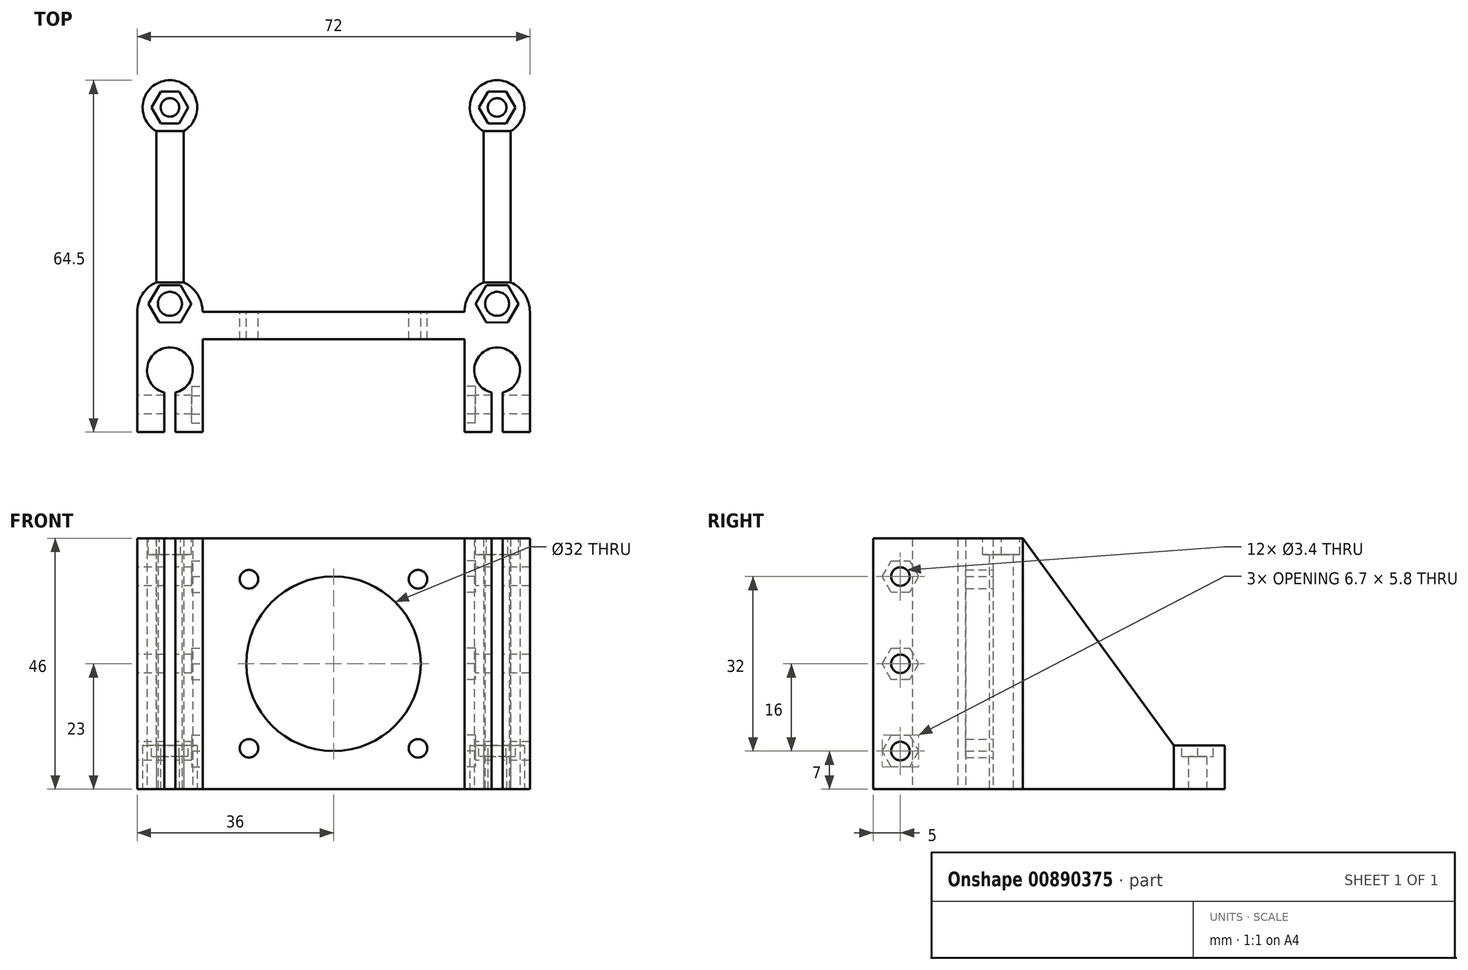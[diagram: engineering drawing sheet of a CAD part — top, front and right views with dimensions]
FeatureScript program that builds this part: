
annotation { "Feature Type Name" : "Feature", "Feature Type Description" : "" }
export const myFeature = defineFeature(function(context is Context, id is Id, definition is map)
    precondition{}
    {
        {
            var Q0;
            Q0=qCreatedBy(makeId("Top.planeOp"),FACE);
            var sketch = newSketch(context, id + "F0", { "sketchPlane" : qUnion([Q0])});
            skArc(sketch, "E0", {"start": v(-29, -14.78) * mm, "mid": v(-30, -6.5) * mm, "end": v(-31, -14.78) * mm});
            skPoint(sketch, "E1.first.point", {"position": v(-36, 0) * mm});
            skLineSegment(sketch, "E2", {"start": v(-36, 0) * mm, "end": v(-36, -22) * mm});
            skLineSegment(sketch, "E3", {"start": v(-36, -22) * mm, "end": v(-31, -22) * mm});
            skLineSegment(sketch, "E4", {"start": v(-31, -22) * mm, "end": v(-31, -14.78) * mm});
            skLineSegment(sketch, "E5", {"start": v(-29, -14.78) * mm, "end": v(-29, -22) * mm});
            skLineSegment(sketch, "E6", {"start": v(-29, -22) * mm, "end": v(-24, -22) * mm});
            skLineSegment(sketch, "E7", {"start": v(0, 0) * mm, "end": v(-24, 0) * mm});
            skLineSegment(sketch, "E8", {"start": v(0, 0) * mm, "end": v(0, -5) * mm});
            skLineSegment(sketch, "E9", {"start": v(0, -5) * mm, "end": v(-24, -5) * mm});
            skLineSegment(sketch, "E10", {"start": v(-24, -5) * mm, "end": v(-24, -22) * mm});
            skLineSegment(sketch, "E11", {"start": v(-30, -10.7) * mm, "end": v(-30, 1.5) * mm, "construction": true});
            skLineSegment(sketch, "E12", {"start": v(-24, 0) * mm, "end": v(-36, 0) * mm, "construction": true});
            skArc(sketch, "E13", {"start": v(-24, 0) * mm, "mid": v(-30, 6) * mm, "end": v(-36, 0) * mm});
            skLineSegment(sketch, "E14.MirrorCS", {"start": v(0, -5) * mm, "end": v(24, -5) * mm});
            skLineSegment(sketch, "E15.MirrorCS", {"start": v(24, 0) * mm, "end": v(36, 0) * mm, "construction": true});
            skLineSegment(sketch, "E16.MirrorCS", {"start": v(29, -22) * mm, "end": v(24, -22) * mm});
            skLineSegment(sketch, "E17.MirrorCS", {"start": v(31, -22) * mm, "end": v(31, -14.78) * mm});
            skLineSegment(sketch, "E18.MirrorCS", {"start": v(29, -14.78) * mm, "end": v(29, -22) * mm});
            skPoint(sketch, "E19.MirrorP", {"position": v(36, 0) * mm});
            skArc(sketch, "E20.MirrorCS", {"start": v(24, 0) * mm, "mid": v(30, 6) * mm, "end": v(36, 0) * mm});
            skArc(sketch, "E21.MirrorC", {"start": v(29, -14.78) * mm, "mid": v(30, -6.5) * mm, "end": v(31, -14.78) * mm});
            skLineSegment(sketch, "E22.MirrorCS", {"start": v(0, 0) * mm, "end": v(24, 0) * mm});
            skLineSegment(sketch, "E23.MirrorCS", {"start": v(24, -5) * mm, "end": v(24, -22) * mm});
            skLineSegment(sketch, "E24.MirrorCS", {"start": v(30, -10.7) * mm, "end": v(30, 1.5) * mm, "construction": true});
            skLineSegment(sketch, "E25.MirrorCS", {"start": v(36, -22) * mm, "end": v(31, -22) * mm});
            skLineSegment(sketch, "E26.MirrorCS", {"start": v(36, 0) * mm, "end": v(36, -22) * mm});
            skCircle(sketch, "E27", {"center": v(-30, 1.5) * mm, "radius": 2.2 * mm});
            skCircle(sketch, "E28.MirrorC", {"center": v(30, 1.5) * mm, "radius": 2.2 * mm});
            skLineSegment(sketch, "E29", {"start": v(-30, 1.5) * mm, "end": v(-30, 46.69) * mm, "construction": true});
            skLineSegment(sketch, "E30", {"start": v(-32.5, 5.45) * mm, "end": v(-32.5, 33.17) * mm});
            skLineSegment(sketch, "E31", {"start": v(-32.5, 33.17) * mm, "end": v(-27.5, 33.17) * mm});
            skLineSegment(sketch, "E32", {"start": v(-27.5, 33.17) * mm, "end": v(-27.5, 5.45) * mm});
            skLineSegment(sketch, "E33", {"start": v(-27.5, 5.45) * mm, "end": v(-32.5, 5.45) * mm, "construction": true});
            skCircle(sketch, "E34", {"center": v(-30, 37.5) * mm, "radius": 1.7 * mm});
            skCircle(sketch, "E35", {"center": v(-30, 37.5) * mm, "radius": 5 * mm});
            skLineSegment(sketch, "E36.MirrorCS", {"start": v(27.5, 33.17) * mm, "end": v(27.5, 5.45) * mm});
            skLineSegment(sketch, "E37.MirrorCS", {"start": v(32.5, 5.45) * mm, "end": v(32.5, 33.17) * mm});
            skCircle(sketch, "E38.MirrorC", {"center": v(30, 37.5) * mm, "radius": 5 * mm});
            skCircle(sketch, "E39.MirrorC", {"center": v(30, 37.5) * mm, "radius": 1.7 * mm});
            skSolve(sketch);
        }
        {
            var Q0;
            Q0=qSketchRegion(id+"F0",true);
            extrude(context, id + "F1", {"entities" : qUnion([Q0]), "depth" : 46 * mm, "offsetDistance" : 25 * mm});
        }
        {
            var Q0;
            Q0=makeQuery(id+"F1.opExtrude","CAP_FACE",FACE,{"disambiguationData":[OSD([sQuery(id+"F0.wireOp",EDGE,"E0"),sQuery(id+"F0.wireOp",EDGE,"E2"),sQuery(id+"F0.wireOp",EDGE,"E3"),sQuery(id+"F0.wireOp",EDGE,"E4"),sQuery(id+"F0.wireOp",EDGE,"E5"),sQuery(id+"F0.wireOp",EDGE,"E6"),sQuery(id+"F0.wireOp",EDGE,"E7"),sQuery(id+"F0.wireOp",EDGE,"E9"),sQuery(id+"F0.wireOp",EDGE,"E10"),sQuery(id+"F0.wireOp",EDGE,"E13"),sQuery(id+"F0.wireOp",EDGE,"E14.MirrorCS"),sQuery(id+"F0.wireOp",EDGE,"E16.MirrorCS"),sQuery(id+"F0.wireOp",EDGE,"E17.MirrorCS"),sQuery(id+"F0.wireOp",EDGE,"E18.MirrorCS"),sQuery(id+"F0.wireOp",EDGE,"E20.MirrorCS"),sQuery(id+"F0.wireOp",EDGE,"E21.MirrorC"),sQuery(id+"F0.wireOp",EDGE,"E22.MirrorCS"),sQuery(id+"F0.wireOp",EDGE,"E23.MirrorCS"),sQuery(id+"F0.wireOp",EDGE,"E25.MirrorCS"),sQuery(id+"F0.wireOp",EDGE,"E26.MirrorCS"),sQuery(id+"F0.wireOp",EDGE,"E27"),sQuery(id+"F0.wireOp",EDGE,"E28.MirrorC")])],"isStart":false});
            var sketch = newSketch(context, id + "F2", { "sketchPlane" : qUnion([Q0])});
            skCircle(sketch, "E40.cCircle", {"center": v(-30, 1.5) * mm, "radius": 3.4 * mm, "construction": true});
            skLineSegment(sketch, "E40.0", {"start": v(-26.07, 1.48) * mm, "end": v(-28.05, -1.9) * mm});
            skLineSegment(sketch, "E40.1", {"start": v(-28.05, -1.9) * mm, "end": v(-31.98, -1.9) * mm});
            skLineSegment(sketch, "E40.2", {"start": v(-31.98, -1.9) * mm, "end": v(-33.93, 1.52) * mm});
            skLineSegment(sketch, "E40.3", {"start": v(-33.93, 1.52) * mm, "end": v(-31.95, 4.9) * mm});
            skLineSegment(sketch, "E40.4", {"start": v(-31.95, 4.9) * mm, "end": v(-28.02, 4.9) * mm});
            skLineSegment(sketch, "E40.5", {"start": v(-28.02, 4.9) * mm, "end": v(-26.07, 1.48) * mm});
            skPoint(sketch, "E40.0.midPoint", {"position": v(-27.06, -0.21) * mm});
            skPoint(sketch, "E41.MirrorP", {"position": v(27.06, -0.21) * mm});
            skLineSegment(sketch, "E42.MirrorCS", {"start": v(31.95, 4.9) * mm, "end": v(28.02, 4.9) * mm});
            skLineSegment(sketch, "E43.MirrorCS", {"start": v(28.05, -1.9) * mm, "end": v(31.98, -1.9) * mm});
            skLineSegment(sketch, "E44.MirrorCS", {"start": v(31.98, -1.9) * mm, "end": v(33.93, 1.52) * mm});
            skCircle(sketch, "E45.MirrorC", {"center": v(30, 1.5) * mm, "radius": 3.4 * mm, "construction": true});
            skLineSegment(sketch, "E46.MirrorCS", {"start": v(26.07, 1.48) * mm, "end": v(28.05, -1.9) * mm});
            skLineSegment(sketch, "E47.MirrorCS", {"start": v(33.93, 1.52) * mm, "end": v(31.95, 4.9) * mm});
            skLineSegment(sketch, "E48.MirrorCS", {"start": v(28.02, 4.9) * mm, "end": v(26.07, 1.48) * mm});
            skSolve(sketch);
        }
        {
            var Q0;
            Q0=qSketchRegion(id+"F2",true);
            extrude(context, id + "F3", {"entities" : qUnion([Q0]), "operationType" : NewBodyOperationType.REMOVE, "oppositeDirection" : true, "depth" : 3 * mm, "offsetDistance" : 25 * mm});
        }
        {
            var Q0;
            Q0=makeQuery(id+"F1.opExtrude","SWEPT_FACE",FACE,{"disambiguationData":[OSD([sQuery(id+"F0.wireOp",EDGE,"E30")])]});
            cPlane(context, id + "F4", {"entities" : qUnion([Q0]), "cplaneType" : CPlaneType.OFFSET, "offset" : 10 * mm, "width" : 150 * mm, "height" : 150 * mm});
        }
        {
            var Q0;
            Q0=qCreatedBy(id+"F4.planeOp",FACE);
            var sketch = newSketch(context, id + "F5", { "sketchPlane" : qUnion([Q0])});
            skLineSegment(sketch, "E49", {"start": v(-43.17, 8) * mm, "end": v(-33.17, 8) * mm});
            skLineSegment(sketch, "E50", {"start": v(-33.17, 8) * mm, "end": v(-5.45, 46) * mm});
            skLineSegment(sketch, "E51", {"start": v(-5.45, 46) * mm, "end": v(-5.45, 46) * mm});
            skLineSegment(sketch, "E52", {"start": v(-5.45, 46) * mm, "end": v(-43.17, 46) * mm});
            skLineSegment(sketch, "E53", {"start": v(-43.17, 46) * mm, "end": v(-43.17, 8) * mm});
            skCircle(sketch, "E54", {"center": v(17, 39) * mm, "radius": 1.7 * mm});
            skCircle(sketch, "E55", {"center": v(17, 23) * mm, "radius": 1.7 * mm});
            skCircle(sketch, "E56", {"center": v(17, 7) * mm, "radius": 1.7 * mm});
            skSolve(sketch);
        }
        {
            var Q0;
            Q0=qSketchRegion(id+"F5",true);
            extrude(context, id + "F6", {"entities" : qUnion([Q0]), "operationType" : NewBodyOperationType.REMOVE, "endBound" : BoundingType.THROUGH_ALL, "oppositeDirection" : true, "depth" : 25 * mm, "offsetDistance" : 25 * mm});
        }
        {
            var Q0;
            Q0=makeQuery(id+"F6.boolean.opBoolean","COPY",FACE,{"disambiguationData":[TD([makeQuery(id+"F1.opExtrude","SWEPT_FACE",FACE,{"disambiguationData":[OSD([sQuery(id+"F0.wireOp",EDGE,"E30")])]})])],"derivedFrom":makeQuery(id+"F6.opExtrude","SWEPT_FACE",FACE,{"disambiguationData":[OSD([sQuery(id+"F5.wireOp",EDGE,"E49")])]})});
            var sketch = newSketch(context, id + "F7", { "sketchPlane" : qUnion([Q0])});
            skCircle(sketch, "E57.cCircle", {"center": v(-30, 37.5) * mm, "radius": 2.9 * mm, "construction": true});
            skLineSegment(sketch, "E57.0", {"start": v(-26.65, 37.5) * mm, "end": v(-28.33, 34.6) * mm});
            skLineSegment(sketch, "E57.1", {"start": v(-28.33, 34.6) * mm, "end": v(-31.67, 34.6) * mm});
            skLineSegment(sketch, "E57.2", {"start": v(-31.67, 34.6) * mm, "end": v(-33.35, 37.5) * mm});
            skLineSegment(sketch, "E57.3", {"start": v(-33.35, 37.5) * mm, "end": v(-31.67, 40.4) * mm});
            skLineSegment(sketch, "E57.4", {"start": v(-31.67, 40.4) * mm, "end": v(-28.33, 40.4) * mm});
            skLineSegment(sketch, "E57.5", {"start": v(-28.33, 40.4) * mm, "end": v(-26.65, 37.5) * mm});
            skPoint(sketch, "E57.0.midPoint", {"position": v(-27.49, 36.05) * mm});
            skLineSegment(sketch, "E58.MirrorCS", {"start": v(26.65, 37.5) * mm, "end": v(28.33, 34.6) * mm});
            skLineSegment(sketch, "E59.MirrorCS", {"start": v(33.35, 37.5) * mm, "end": v(31.67, 40.4) * mm});
            skLineSegment(sketch, "E60.MirrorCS", {"start": v(31.67, 34.6) * mm, "end": v(33.35, 37.5) * mm});
            skLineSegment(sketch, "E61.MirrorCS", {"start": v(31.67, 40.4) * mm, "end": v(28.33, 40.4) * mm});
            skLineSegment(sketch, "E62.MirrorCS", {"start": v(28.33, 34.6) * mm, "end": v(31.67, 34.6) * mm});
            skPoint(sketch, "E63.MirrorP", {"position": v(27.49, 36.05) * mm});
            skCircle(sketch, "E64.MirrorC", {"center": v(30, 37.5) * mm, "radius": 2.9 * mm, "construction": true});
            skLineSegment(sketch, "E65.MirrorCS", {"start": v(28.33, 40.4) * mm, "end": v(26.65, 37.5) * mm});
            skSolve(sketch);
        }
        {
            var Q0;
            Q0=qSketchRegion(id+"F7",true);
            extrude(context, id + "F8", {"entities" : qUnion([Q0]), "operationType" : NewBodyOperationType.REMOVE, "oppositeDirection" : true, "depth" : 2 * mm, "offsetDistance" : 25 * mm});
        }
        {
            var Q0;
            Q0=makeQuery(id+"F1.opExtrude","SWEPT_FACE",FACE,{"disambiguationData":[OSD([sQuery(id+"F0.wireOp",EDGE,"E23.MirrorCS")])]});
            var sketch = newSketch(context, id + "F9", { "sketchPlane" : qUnion([Q0])});
            skCircle(sketch, "E66.cCircle", {"center": v(17, 39) * mm, "radius": 2.9 * mm, "construction": true});
            skLineSegment(sketch, "E66.0", {"start": v(18.67, 36.1) * mm, "end": v(15.33, 36.1) * mm});
            skLineSegment(sketch, "E66.1", {"start": v(15.33, 36.1) * mm, "end": v(13.65, 39) * mm});
            skLineSegment(sketch, "E66.2", {"start": v(13.65, 39) * mm, "end": v(15.33, 41.9) * mm});
            skLineSegment(sketch, "E66.3", {"start": v(15.33, 41.9) * mm, "end": v(18.67, 41.9) * mm});
            skLineSegment(sketch, "E66.4", {"start": v(18.67, 41.9) * mm, "end": v(20.35, 39) * mm});
            skLineSegment(sketch, "E66.5", {"start": v(20.35, 39) * mm, "end": v(18.67, 36.1) * mm});
            skPoint(sketch, "E66.0.midPoint", {"position": v(17, 36.1) * mm});
            skCircle(sketch, "E67.cCircle", {"center": v(17, 23) * mm, "radius": 2.9 * mm, "construction": true});
            skLineSegment(sketch, "E67.0", {"start": v(18.67, 20.1) * mm, "end": v(15.33, 20.1) * mm});
            skLineSegment(sketch, "E67.1", {"start": v(15.33, 20.1) * mm, "end": v(13.65, 23) * mm});
            skLineSegment(sketch, "E67.2", {"start": v(13.65, 23) * mm, "end": v(15.33, 25.9) * mm});
            skLineSegment(sketch, "E67.3", {"start": v(15.33, 25.9) * mm, "end": v(18.67, 25.9) * mm});
            skLineSegment(sketch, "E67.4", {"start": v(18.67, 25.9) * mm, "end": v(20.35, 23) * mm});
            skLineSegment(sketch, "E67.5", {"start": v(20.35, 23) * mm, "end": v(18.67, 20.1) * mm});
            skPoint(sketch, "E67.0.midPoint", {"position": v(17, 20.1) * mm});
            skCircle(sketch, "E68.cCircle", {"center": v(17, 7) * mm, "radius": 2.9 * mm, "construction": true});
            skLineSegment(sketch, "E68.0", {"start": v(18.67, 4.1) * mm, "end": v(15.33, 4.1) * mm});
            skLineSegment(sketch, "E68.1", {"start": v(15.33, 4.1) * mm, "end": v(13.65, 7) * mm});
            skLineSegment(sketch, "E68.2", {"start": v(13.65, 7) * mm, "end": v(15.33, 9.9) * mm});
            skLineSegment(sketch, "E68.3", {"start": v(15.33, 9.9) * mm, "end": v(18.67, 9.9) * mm});
            skLineSegment(sketch, "E68.4", {"start": v(18.67, 9.9) * mm, "end": v(20.35, 7) * mm});
            skLineSegment(sketch, "E68.5", {"start": v(20.35, 7) * mm, "end": v(18.67, 4.1) * mm});
            skPoint(sketch, "E68.0.midPoint", {"position": v(17, 4.1) * mm});
            skSolve(sketch);
        }
        {
            var Q0;
            Q0=qSketchRegion(id+"F9",true);
            extrude(context, id + "F10", {"entities" : qUnion([Q0]), "operationType" : NewBodyOperationType.REMOVE, "oppositeDirection" : true, "depth" : 2 * mm, "offsetDistance" : 25 * mm});
        }
        {
            var Q0;
            Q0=makeQuery(id+"F1.opExtrude","SWEPT_FACE",FACE,{"disambiguationData":[OSD([sQuery(id+"F0.wireOp",EDGE,"E10")])]});
            var sketch = newSketch(context, id + "F11", { "sketchPlane" : qUnion([Q0])});
            skCircle(sketch, "E69.cCircle", {"center": v(-17, 39) * mm, "radius": 2.9 * mm, "construction": true});
            skLineSegment(sketch, "E69.0", {"start": v(-15.33, 36.1) * mm, "end": v(-18.67, 36.1) * mm});
            skLineSegment(sketch, "E69.1", {"start": v(-18.67, 36.1) * mm, "end": v(-20.35, 39) * mm});
            skLineSegment(sketch, "E69.2", {"start": v(-20.35, 39) * mm, "end": v(-18.67, 41.9) * mm});
            skLineSegment(sketch, "E69.3", {"start": v(-18.67, 41.9) * mm, "end": v(-15.33, 41.9) * mm});
            skLineSegment(sketch, "E69.4", {"start": v(-15.33, 41.9) * mm, "end": v(-13.65, 39) * mm});
            skLineSegment(sketch, "E69.5", {"start": v(-13.65, 39) * mm, "end": v(-15.33, 36.1) * mm});
            skPoint(sketch, "E69.0.midPoint", {"position": v(-17, 36.1) * mm});
            skCircle(sketch, "E70.cCircle", {"center": v(-17, 23) * mm, "radius": 2.9 * mm, "construction": true});
            skLineSegment(sketch, "E70.0", {"start": v(-15.33, 20.1) * mm, "end": v(-18.67, 20.1) * mm});
            skLineSegment(sketch, "E70.1", {"start": v(-18.67, 20.1) * mm, "end": v(-20.35, 23) * mm});
            skLineSegment(sketch, "E70.2", {"start": v(-20.35, 23) * mm, "end": v(-18.67, 25.9) * mm});
            skLineSegment(sketch, "E70.3", {"start": v(-18.67, 25.9) * mm, "end": v(-15.33, 25.9) * mm});
            skLineSegment(sketch, "E70.4", {"start": v(-15.33, 25.9) * mm, "end": v(-13.65, 23) * mm});
            skLineSegment(sketch, "E70.5", {"start": v(-13.65, 23) * mm, "end": v(-15.33, 20.1) * mm});
            skPoint(sketch, "E70.0.midPoint", {"position": v(-17, 20.1) * mm});
            skCircle(sketch, "E71.cCircle", {"center": v(-17, 7) * mm, "radius": 2.9 * mm, "construction": true});
            skLineSegment(sketch, "E71.0", {"start": v(-15.33, 4.1) * mm, "end": v(-18.67, 4.1) * mm});
            skLineSegment(sketch, "E71.1", {"start": v(-18.67, 4.1) * mm, "end": v(-20.35, 7) * mm});
            skLineSegment(sketch, "E71.2", {"start": v(-20.35, 7) * mm, "end": v(-18.67, 9.9) * mm});
            skLineSegment(sketch, "E71.3", {"start": v(-18.67, 9.9) * mm, "end": v(-15.33, 9.9) * mm});
            skLineSegment(sketch, "E71.4", {"start": v(-15.33, 9.9) * mm, "end": v(-13.65, 7) * mm});
            skLineSegment(sketch, "E71.5", {"start": v(-13.65, 7) * mm, "end": v(-15.33, 4.1) * mm});
            skPoint(sketch, "E71.0.midPoint", {"position": v(-17, 4.1) * mm});
            skSolve(sketch);
        }
        {
            var Q0;
            Q0=qSketchRegion(id+"F11",true);
            extrude(context, id + "F12", {"entities" : qUnion([Q0]), "operationType" : NewBodyOperationType.REMOVE, "oppositeDirection" : true, "depth" : 2 * mm, "offsetDistance" : 25 * mm});
        }
        {
            var Q0;
            Q0=makeQuery(id+"F1.opExtrude","SWEPT_FACE",FACE,{"disambiguationData":[OSD([sQuery(id+"F0.wireOp",EDGE,"E7"),sQuery(id+"F0.wireOp",EDGE,"E22.MirrorCS")])]});
            var sketch = newSketch(context, id + "F13", { "sketchPlane" : qUnion([Q0])});
            skCircle(sketch, "E72", {"center": v(0, 23) * mm, "radius": 16 * mm});
            skPoint(sketch, "E72.centerSnap0", {"position": v(24, 23) * mm});
            skPoint(sketch, "E73", {"position": v(-15.5, 38.5) * mm});
            skPoint(sketch, "E74", {"position": v(15.5, 38.5) * mm});
            skPoint(sketch, "E75", {"position": v(15.5, 7.5) * mm});
            skPoint(sketch, "E76", {"position": v(-15.5, 7.5) * mm});
            skSolve(sketch);
        }
        {
            var Q0;
            Q0=makeQuery(id+"F13.imprint","IMPRINT",FACE,{"disambiguationData":[TD([[makeQuery(id+"F13.imprint","IMPRINT",EDGE,{"derivedFrom":sQuery(id+"F13.wireOp",EDGE,"E72")}),1.0]])]});
            var Q1;
            Q1=makeQuery(id+"F1.opExtrude","SWEPT_FACE",FACE,{"disambiguationData":[OSD([sQuery(id+"F0.wireOp",EDGE,"E9"),sQuery(id+"F0.wireOp",EDGE,"E14.MirrorCS")])]});
            extrude(context, id + "F14", {"entities" : qUnion([Q0]), "operationType" : NewBodyOperationType.REMOVE, "endBound" : BoundingType.UP_TO_SURFACE, "oppositeDirection" : true, "depth" : 25 * mm, "endBoundEntityFace" : qUnion([Q1]), "offsetDistance" : 25 * mm});
        }
        {
            var Q0;
            Q0=sQuery(id+"F13.wireOp",VERTEX,"E73");
            var Q1;
            Q1=sQuery(id+"F13.wireOp",VERTEX,"E74");
            var Q2;
            Q2=sQuery(id+"F13.wireOp",VERTEX,"E75");
            var Q3;
            Q3=sQuery(id+"F13.wireOp",VERTEX,"E76");
            var Q4;
            Q4=makeQuery(id+"F1.opExtrude","SWEPT_BODY",BODY,{"disambiguationData":[OSD([sQuery(id+"F0.wireOp",EDGE,"E0"),sQuery(id+"F0.wireOp",EDGE,"E2"),sQuery(id+"F0.wireOp",EDGE,"E3"),sQuery(id+"F0.wireOp",EDGE,"E4"),sQuery(id+"F0.wireOp",EDGE,"E5"),sQuery(id+"F0.wireOp",EDGE,"E6"),sQuery(id+"F0.wireOp",EDGE,"E7"),sQuery(id+"F0.wireOp",EDGE,"E9"),sQuery(id+"F0.wireOp",EDGE,"E10"),sQuery(id+"F0.wireOp",EDGE,"E13"),sQuery(id+"F0.wireOp",EDGE,"E14.MirrorCS"),sQuery(id+"F0.wireOp",EDGE,"E16.MirrorCS"),sQuery(id+"F0.wireOp",EDGE,"E17.MirrorCS"),sQuery(id+"F0.wireOp",EDGE,"E18.MirrorCS"),sQuery(id+"F0.wireOp",EDGE,"E20.MirrorCS"),sQuery(id+"F0.wireOp",EDGE,"E21.MirrorC"),sQuery(id+"F0.wireOp",EDGE,"E22.MirrorCS"),sQuery(id+"F0.wireOp",EDGE,"E23.MirrorCS"),sQuery(id+"F0.wireOp",EDGE,"E25.MirrorCS"),sQuery(id+"F0.wireOp",EDGE,"E26.MirrorCS"),sQuery(id+"F0.wireOp",EDGE,"E27"),sQuery(id+"F0.wireOp",EDGE,"E28.MirrorC"),sQuery(id+"F0.wireOp",EDGE,"E30"),sQuery(id+"F0.wireOp",EDGE,"E32"),sQuery(id+"F0.wireOp",EDGE,"E34"),sQuery(id+"F0.wireOp",EDGE,"E35"),sQuery(id+"F0.wireOp",EDGE,"E36.MirrorCS"),sQuery(id+"F0.wireOp",EDGE,"E37.MirrorCS"),sQuery(id+"F0.wireOp",EDGE,"E38.MirrorC"),sQuery(id+"F0.wireOp",EDGE,"E39.MirrorC")])]});
            hole(context, id + "F15", {"style" : HoleStyle.SIMPLE, "endStyle" : HoleEndStyle.THROUGH, "standardTappedOrClearance" : lookupTablePath({ "fit" : "Normal", "standard" : "ISO", "size" : "M3", "type" : "Clearance" }), "standardBlindInLast" : lookupTablePath({ "fit" : "Normal", "standard" : "ISO", "size" : "M3", "type" : "Clearance" }), "holeDiameter" : 3.4 * mm, "majorDiameter" : 5 * mm, "isTappedThrough" : true, "tappedDepth" : 12 * mm, "tapClearance" : 3, "locations" : qUnion([Q0, Q1, Q2, Q3]), "scope" : qUnion([Q4])});
        }
    });
